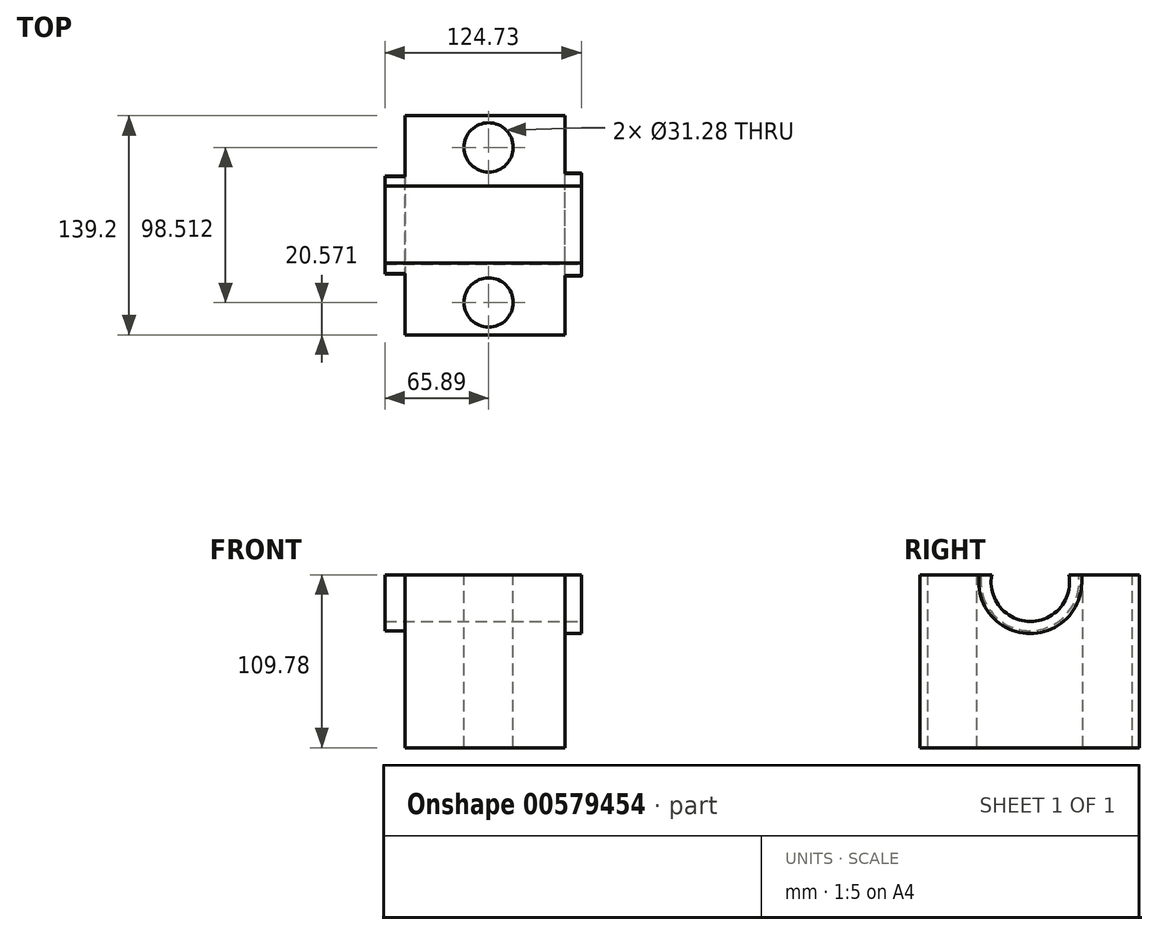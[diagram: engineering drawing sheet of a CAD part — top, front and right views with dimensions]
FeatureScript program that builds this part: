
annotation { "Feature Type Name" : "Feature", "Feature Type Description" : "" }
export const myFeature = defineFeature(function(context is Context, id is Id, definition is map)
    precondition{}
    {
        {
            var Q0;
            Q0=qCreatedBy(makeId("Front.planeOp"),FACE);
            var sketch = newSketch(context, id + "F0", { "sketchPlane" : qUnion([Q0])});
            skLineSegment(sketch, "E0.bottom", {"start": v(-52.94, 47.52) * mm, "end": v(48.43, 47.52) * mm});
            skLineSegment(sketch, "E0.top", {"start": v(-52.94, -62.26) * mm, "end": v(48.43, -62.26) * mm});
            skLineSegment(sketch, "E0.left", {"start": v(-52.94, 47.52) * mm, "end": v(-52.94, -62.26) * mm});
            skLineSegment(sketch, "E0.right", {"start": v(48.43, 47.52) * mm, "end": v(48.43, -62.26) * mm});
            skSolve(sketch);
        }
        {
            var Q0;
            Q0=makeQuery(id+"F0.imprint","IMPRINT",FACE,{"disambiguationData":[TD([[makeQuery(id+"F0.imprint","IMPRINT",EDGE,{"derivedFrom":sQuery(id+"F0.wireOp",EDGE,"E0.bottom")}),-1.0]])]});
            extrude(context, id + "F1", {"entities" : qUnion([Q0]), "endBound" : BoundingType.SYMMETRIC, "depth" : 139.2 * mm, "offsetDistance" : 25.4 * mm});
        }
        {
            var Q0;
            Q0=makeQuery(id+"F1.opExtrude","SWEPT_FACE",FACE,{"disambiguationData":[OSD([sQuery(id+"F0.wireOp",EDGE,"E0.right")])]});
            var sketch = newSketch(context, id + "F2", { "sketchPlane" : qUnion([Q0])});
            skArc(sketch, "E1", {"start": v(-24.06, 47.52) * mm, "mid": v(0.45, 18) * mm, "end": v(24.97, 47.52) * mm});
            skArc(sketch, "E2", {"start": v(-34.3, 47.52) * mm, "mid": v(0.3, 8.1) * mm, "end": v(34.9, 47.52) * mm});
            skSolve(sketch);
        }
        {
            var Q0;
            {var subQ0=sQuery(id+"F2.wireOp",EDGE,"E1");Q0=makeQuery(id+"F2.imprint","IMPRINT",FACE,{"disambiguationData":[TD([[makeQuery(id+"F2.imprint","IMPRINT",EDGE,{"derivedFrom":subQ0}),1.0]])]});}
            extrude(context, id + "F3", {"entities" : qUnion([Q0]), "operationType" : NewBodyOperationType.REMOVE, "endBound" : BoundingType.THROUGH_ALL, "oppositeDirection" : true, "depth" : 25.4 * mm, "offsetDistance" : 25.4 * mm});
        }
        {
            var Q0;
            Q0=makeQuery(id+"F1.opExtrude","SWEPT_FACE",FACE,{"disambiguationData":[OSD([sQuery(id+"F0.wireOp",EDGE,"E0.right")])]});
            var sketch = newSketch(context, id + "F4", { "sketchPlane" : qUnion([Q0])});
            skArc(sketch, "E3", {"start": v(-32.03, 47.52) * mm, "mid": v(0.37, 10.33) * mm, "end": v(32.77, 47.52) * mm});
            skSolve(sketch);
        }
        {
            var Q0;
            {var subQ0=sQuery(id+"F4.wireOp",EDGE,"E3");Q0=makeQuery(id+"F4.imprint","IMPRINT",FACE,{"disambiguationData":[TD([[makeQuery(id+"F4.imprint","IMPRINT",EDGE,{"derivedFrom":subQ0}),1.0]])]});}
            extrude(context, id + "F5", {"entities" : qUnion([Q0]), "operationType" : NewBodyOperationType.ADD, "depth" : 10.4 * mm, "offsetDistance" : 25.4 * mm});
        }
        {
            var Q0;
            Q0=makeQuery(id+"F1.opExtrude","SWEPT_FACE",FACE,{"disambiguationData":[OSD([sQuery(id+"F0.wireOp",EDGE,"E0.left")])]});
            var sketch = newSketch(context, id + "F6", { "sketchPlane" : qUnion([Q0])});
            skArc(sketch, "E4", {"start": v(-30.98, 47.52) * mm, "mid": v(-0.15, 12.12) * mm, "end": v(30.68, 47.52) * mm});
            skSolve(sketch);
        }
        {
            var Q0;
            {var subQ0=sQuery(id+"F6.wireOp",EDGE,"E4");Q0=makeQuery(id+"F6.imprint","IMPRINT",FACE,{"disambiguationData":[TD([[makeQuery(id+"F6.imprint","IMPRINT",EDGE,{"derivedFrom":subQ0}),1.0]])]});}
            extrude(context, id + "F7", {"entities" : qUnion([Q0]), "operationType" : NewBodyOperationType.ADD, "depth" : 12.95 * mm, "offsetDistance" : 25.4 * mm});
        }
        {
            var Q0;
            {var subQ0=sQuery(id+"F0.wireOp",EDGE,"E0.bottom");var subQ1=makeQuery(id+"F1.opExtrude","SWEPT_FACE",FACE,{"disambiguationData":[OSD([subQ0])]});var subQ2=sQuery(id+"F0.wireOp",EDGE,"E0.right");var subQ3=sQuery(id+"F0.wireOp",EDGE,"E0.left");var subQ4=makeQuery(id+"F1.opExtrude","CAP_FACE",FACE,{"disambiguationData":[OSD([subQ0,sQuery(id+"F0.wireOp",EDGE,"E0.top"),subQ3,subQ2])],"isStart":true});var subQ6=sQuery(id+"F2.wireOp",EDGE,"E1");var subQ8=makeQuery(id+"F3.boolean.opBoolean","SPLIT",EDGE,{"disambiguationData":[TD([subQ4])],"derivedFrom":makeQuery(id+"F1.opExtrude","SWEPT_EDGE",EDGE,{"disambiguationData":[OSD([subQ0,subQ3])]})});var subQ10=makeQuery(id+"F3.boolean.opBoolean","SPLIT",EDGE,{"disambiguationData":[TD([subQ4])],"derivedFrom":makeQuery(id+"F1.opExtrude","SWEPT_EDGE",EDGE,{"disambiguationData":[OSD([subQ0,subQ2])]})});Q0=makeQuery(id+"F7.boolean.opBoolean","MERGE",FACE,{"derivedFrom":[makeQuery(id+"F5.boolean.opBoolean","MERGE",FACE,{"derivedFrom":[makeQuery(id+"F3.boolean.opBoolean","SPLIT",FACE,{"disambiguationData":[TD([subQ4])],"derivedFrom":subQ1}),makeQuery(id+"F5.opExtrude","SWEPT_FACE",FACE,{"disambiguationData":[OSD([subQ0,subQ2]),TDD([makeQuery(id+"F4.imprint","IMPRINT",EDGE,{"disambiguationData":[TD([[makeQuery(id+"F4.imprint","INTERSECT",VERTEX,{"derivedFrom":[makeQuery(id+"F3.boolean.opBoolean","COPY",EDGE,{"derivedFrom":makeQuery(id+"F3.opExtrude","CAP_EDGE",EDGE,{"disambiguationData":[OSD([subQ6])],"isStart":true})}),subQ10]}),-1.0]])],"derivedFrom":subQ10})])]})]}),makeQuery(id+"F7.opExtrude","SWEPT_FACE",FACE,{"disambiguationData":[OSD([subQ0,subQ3]),TDD([makeQuery(id+"F6.imprint","IMPRINT",EDGE,{"disambiguationData":[TD([[makeQuery(id+"F6.imprint","INTERSECT",VERTEX,{"derivedFrom":[subQ8,sQuery(id+"F6.wireOp",EDGE,"E4")]}),1.0]])],"derivedFrom":subQ8})])]})]});}
            var sketch = newSketch(context, id + "F8", { "sketchPlane" : qUnion([Q0])});
            skCircle(sketch, "E5", {"center": v(0, 49.48) * mm, "radius": 15.64 * mm});
            skCircle(sketch, "E6", {"center": v(0, -49.03) * mm, "radius": 15.64 * mm});
            skSolve(sketch);
        }
        {
            var Q0;
            Q0=makeQuery(id+"F8.imprint","IMPRINT",FACE,{"disambiguationData":[TD([[makeQuery(id+"F8.imprint","IMPRINT",EDGE,{"derivedFrom":sQuery(id+"F8.wireOp",EDGE,"E5")}),1.0]])]});
            var Q1;
            Q1=makeQuery(id+"F8.imprint","IMPRINT",FACE,{"disambiguationData":[TD([[makeQuery(id+"F8.imprint","IMPRINT",EDGE,{"derivedFrom":sQuery(id+"F8.wireOp",EDGE,"E6")}),1.0]])]});
            extrude(context, id + "F9", {"entities" : qUnion([Q0, Q1]), "operationType" : NewBodyOperationType.REMOVE, "endBound" : BoundingType.THROUGH_ALL, "oppositeDirection" : true, "depth" : 25.4 * mm, "offsetDistance" : 25.4 * mm});
        }
    });
